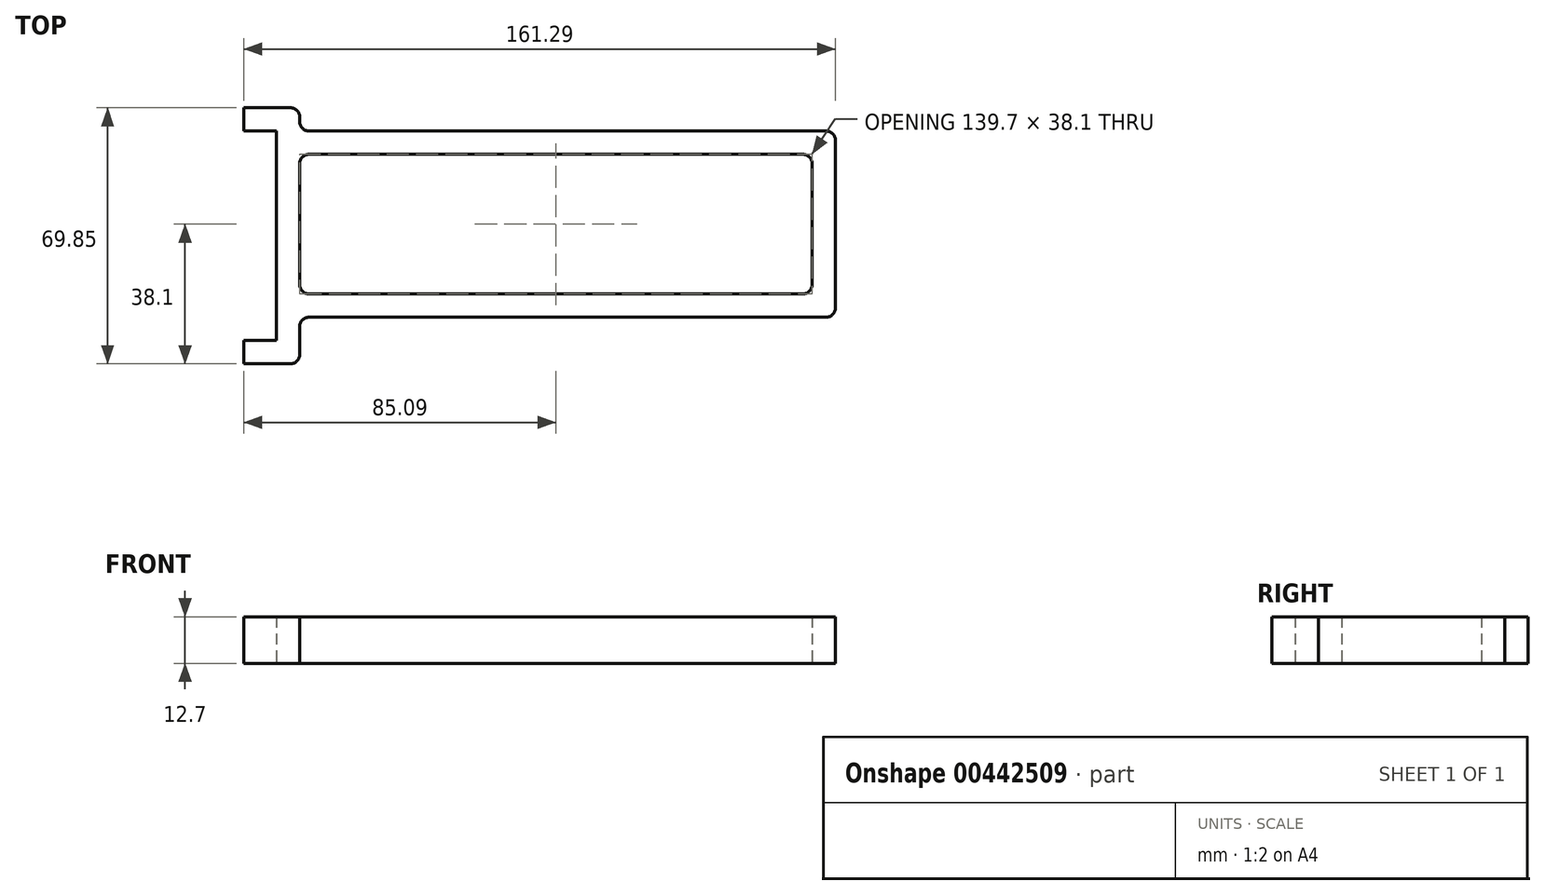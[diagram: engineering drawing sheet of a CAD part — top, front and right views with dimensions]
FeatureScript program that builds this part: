
annotation { "Feature Type Name" : "Feature", "Feature Type Description" : "" }
export const myFeature = defineFeature(function(context is Context, id is Id, definition is map)
    precondition{}
    {
        {
            var Q0;
            Q0=qCreatedBy(makeId("Top.planeOp"),FACE);
            var sketch = newSketch(context, id + "F0", { "sketchPlane" : qUnion([Q0])});
            skLineSegment(sketch, "E0.bottom", {"start": v(-69.85, 19.05) * mm, "end": v(69.85, 19.05) * mm});
            skLineSegment(sketch, "E0.top", {"start": v(-69.85, -19.05) * mm, "end": v(69.85, -19.05) * mm});
            skLineSegment(sketch, "E0.left", {"start": v(-69.85, 19.05) * mm, "end": v(-69.85, -19.05) * mm});
            skLineSegment(sketch, "E0.right", {"start": v(69.85, 19.05) * mm, "end": v(69.85, -19.05) * mm});
            skLineSegment(sketch, "E1", {"start": v(-69.85, 19.05) * mm, "end": v(69.85, -19.05) * mm, "construction": true});
            skLineSegment(sketch, "E2.0", {"start": v(76.2, 25.4) * mm, "end": v(76.2, -25.4) * mm});
            skLineSegment(sketch, "E2.1", {"start": v(-76.2, 25.4) * mm, "end": v(76.2, 25.4) * mm});
            skLineSegment(sketch, "E2.2", {"start": v(-76.2, 25.4) * mm, "end": v(-76.2, -25.4) * mm});
            skLineSegment(sketch, "E2.3", {"start": v(-76.2, -25.4) * mm, "end": v(76.2, -25.4) * mm});
            skSolve(sketch);
        }
        {
            var Q0;
            Q0=qSketchRegion(id+"F0",true);
            extrude(context, id + "F1", {"entities" : qUnion([Q0]), "depth" : 12.7 * mm});
        }
        {
            var Q0;
            Q0=qCreatedBy(makeId("Top.planeOp"),FACE);
            var sketch = newSketch(context, id + "F2", { "sketchPlane" : qUnion([Q0])});
            skLineSegment(sketch, "E3", {"start": v(-69.85, 31.75) * mm, "end": v(-97.8, 31.75) * mm});
            skLineSegment(sketch, "E4", {"start": v(-97.8, 31.75) * mm, "end": v(-97.8, -38.1) * mm});
            skLineSegment(sketch, "E5", {"start": v(-97.8, -38.1) * mm, "end": v(-69.85, -38.1) * mm});
            skLineSegment(sketch, "E6", {"start": v(-69.85, 31.75) * mm, "end": v(-69.85, -38.1) * mm});
            skLineSegment(sketch, "E7.bottom", {"start": v(-85.1, 25.4) * mm, "end": v(-76.2, 25.4) * mm});
            skLineSegment(sketch, "E7.top", {"start": v(-85.1, -31.75) * mm, "end": v(-76.2, -31.75) * mm});
            skLineSegment(sketch, "E7.left", {"start": v(-85.1, 25.4) * mm, "end": v(-85.1, -31.75) * mm});
            skLineSegment(sketch, "E7.right", {"start": v(-76.2, 25.4) * mm, "end": v(-76.2, -31.75) * mm});
            skSolve(sketch);
        }
        {
            var Q0;
            Q0=qSketchRegion(id+"F2",true);
            extrude(context, id + "F3", {"entities" : qUnion([Q0]), "operationType" : NewBodyOperationType.ADD, "depth" : 12.7 * mm});
        }
        {
            var Q0;
            Q0=makeQuery(id+"F1.opExtrude","SWEPT_EDGE",EDGE,{"disambiguationData":[OSD([sQuery(id+"F0.wireOp",EDGE,"E0.bottom"),sQuery(id+"F0.wireOp",EDGE,"E0.left")])]});
            var Q1;
            Q1=makeQuery(id+"F1.opExtrude","SWEPT_EDGE",EDGE,{"disambiguationData":[OSD([sQuery(id+"F0.wireOp",EDGE,"E0.bottom"),sQuery(id+"F0.wireOp",EDGE,"E0.right")])]});
            var Q2;
            Q2=makeQuery(id+"F1.opExtrude","SWEPT_EDGE",EDGE,{"disambiguationData":[OSD([sQuery(id+"F0.wireOp",EDGE,"E0.top"),sQuery(id+"F0.wireOp",EDGE,"E0.right")])]});
            var Q3;
            Q3=makeQuery(id+"F1.opExtrude","SWEPT_EDGE",EDGE,{"disambiguationData":[OSD([sQuery(id+"F0.wireOp",EDGE,"E0.top"),sQuery(id+"F0.wireOp",EDGE,"E0.left")])]});
            var Q4;
            Q4=makeQuery(id+"F3.boolean.opBoolean","INTERSECT",EDGE,{"derivedFrom":[makeQuery(id+"F1.opExtrude","SWEPT_FACE",FACE,{"disambiguationData":[OSD([sQuery(id+"F0.wireOp",EDGE,"E2.1")])]}),makeQuery(id+"F3.opExtrude","SWEPT_FACE",FACE,{"disambiguationData":[OSD([sQuery(id+"F2.wireOp",EDGE,"E6")])]})]});
            var Q5;
            Q5=makeQuery(id+"F1.opExtrude","SWEPT_EDGE",EDGE,{"disambiguationData":[OSD([sQuery(id+"F0.wireOp",EDGE,"E2.0"),sQuery(id+"F0.wireOp",EDGE,"E2.1")])]});
            var Q6;
            Q6=makeQuery(id+"F1.opExtrude","SWEPT_EDGE",EDGE,{"disambiguationData":[OSD([sQuery(id+"F0.wireOp",EDGE,"E2.0"),sQuery(id+"F0.wireOp",EDGE,"E2.3")])]});
            var Q7;
            Q7=makeQuery(id+"F3.boolean.opBoolean","INTERSECT",EDGE,{"derivedFrom":[makeQuery(id+"F1.opExtrude","SWEPT_FACE",FACE,{"disambiguationData":[OSD([sQuery(id+"F0.wireOp",EDGE,"E2.3")])]}),makeQuery(id+"F3.opExtrude","SWEPT_FACE",FACE,{"disambiguationData":[OSD([sQuery(id+"F2.wireOp",EDGE,"E6")])]})]});
            var Q8;
            Q8=makeQuery(id+"F3.opExtrude","SWEPT_EDGE",EDGE,{"disambiguationData":[OSD([sQuery(id+"F2.wireOp",EDGE,"E3"),sQuery(id+"F2.wireOp",EDGE,"E6")])]});
            var Q9;
            Q9=makeQuery(id+"F3.opExtrude","SWEPT_EDGE",EDGE,{"disambiguationData":[OSD([sQuery(id+"F2.wireOp",EDGE,"E5"),sQuery(id+"F2.wireOp",EDGE,"E6")])]});
            fillet(context, id + "F4", {"entities" : qUnion([Q0, Q1, Q2, Q3, Q4, Q5, Q6, Q7, Q8, Q9]), "radius" : 2.54 * mm, "tangentPropagation" : true, "allowEdgeOverflow" : false});
        }
        {
            var Q0;
            Q0=makeQuery(id+"F3.boolean.opBoolean","MERGE",FACE,{"derivedFrom":[makeQuery(id+"F1.opExtrude","CAP_FACE",FACE,{"disambiguationData":[OSD([sQuery(id+"F0.wireOp",EDGE,"E0.bottom"),sQuery(id+"F0.wireOp",EDGE,"E0.top"),sQuery(id+"F0.wireOp",EDGE,"E0.left"),sQuery(id+"F0.wireOp",EDGE,"E0.right"),sQuery(id+"F0.wireOp",EDGE,"E2.0"),sQuery(id+"F0.wireOp",EDGE,"E2.1"),sQuery(id+"F0.wireOp",EDGE,"E2.2"),sQuery(id+"F0.wireOp",EDGE,"E2.3")])],"isStart":true}),makeQuery(id+"F3.opExtrude","CAP_FACE",FACE,{"disambiguationData":[OSD([sQuery(id+"F2.wireOp",EDGE,"E3"),sQuery(id+"F2.wireOp",EDGE,"E4"),sQuery(id+"F2.wireOp",EDGE,"E5"),sQuery(id+"F2.wireOp",EDGE,"E6"),sQuery(id+"F2.wireOp",EDGE,"E7.bottom"),sQuery(id+"F2.wireOp",EDGE,"E7.top"),sQuery(id+"F2.wireOp",EDGE,"E7.left"),sQuery(id+"F2.wireOp",EDGE,"E7.right")])],"isStart":true})]});
            var sketch = newSketch(context, id + "F5", { "sketchPlane" : qUnion([Q0])});
            skLineSegment(sketch, "E8.bottom", {"start": v(-85.1, -31.75) * mm, "end": v(-97.8, -31.75) * mm});
            skLineSegment(sketch, "E8.top", {"start": v(-85.1, 38.1) * mm, "end": v(-97.8, 38.1) * mm});
            skLineSegment(sketch, "E8.left", {"start": v(-85.1, -31.75) * mm, "end": v(-85.1, 38.1) * mm});
            skLineSegment(sketch, "E8.right", {"start": v(-97.8, -31.75) * mm, "end": v(-97.8, 38.1) * mm});
            skSolve(sketch);
        }
        {
            var Q0;
            {var subQ3=sQuery(id+"F5.wireOp",EDGE,"E8.bottom");Q0=makeQuery(id+"F5.imprint","IMPRINT",FACE,{"disambiguationData":[TD([[makeQuery(id+"F5.imprint","IMPRINT",EDGE,{"derivedFrom":subQ3}),-1.0]])]});}
            extrude(context, id + "F6", {"entities" : qUnion([Q0]), "operationType" : NewBodyOperationType.REMOVE, "endBound" : BoundingType.THROUGH_ALL, "oppositeDirection" : true, "depth" : 25.4 * mm});
        }
    });
